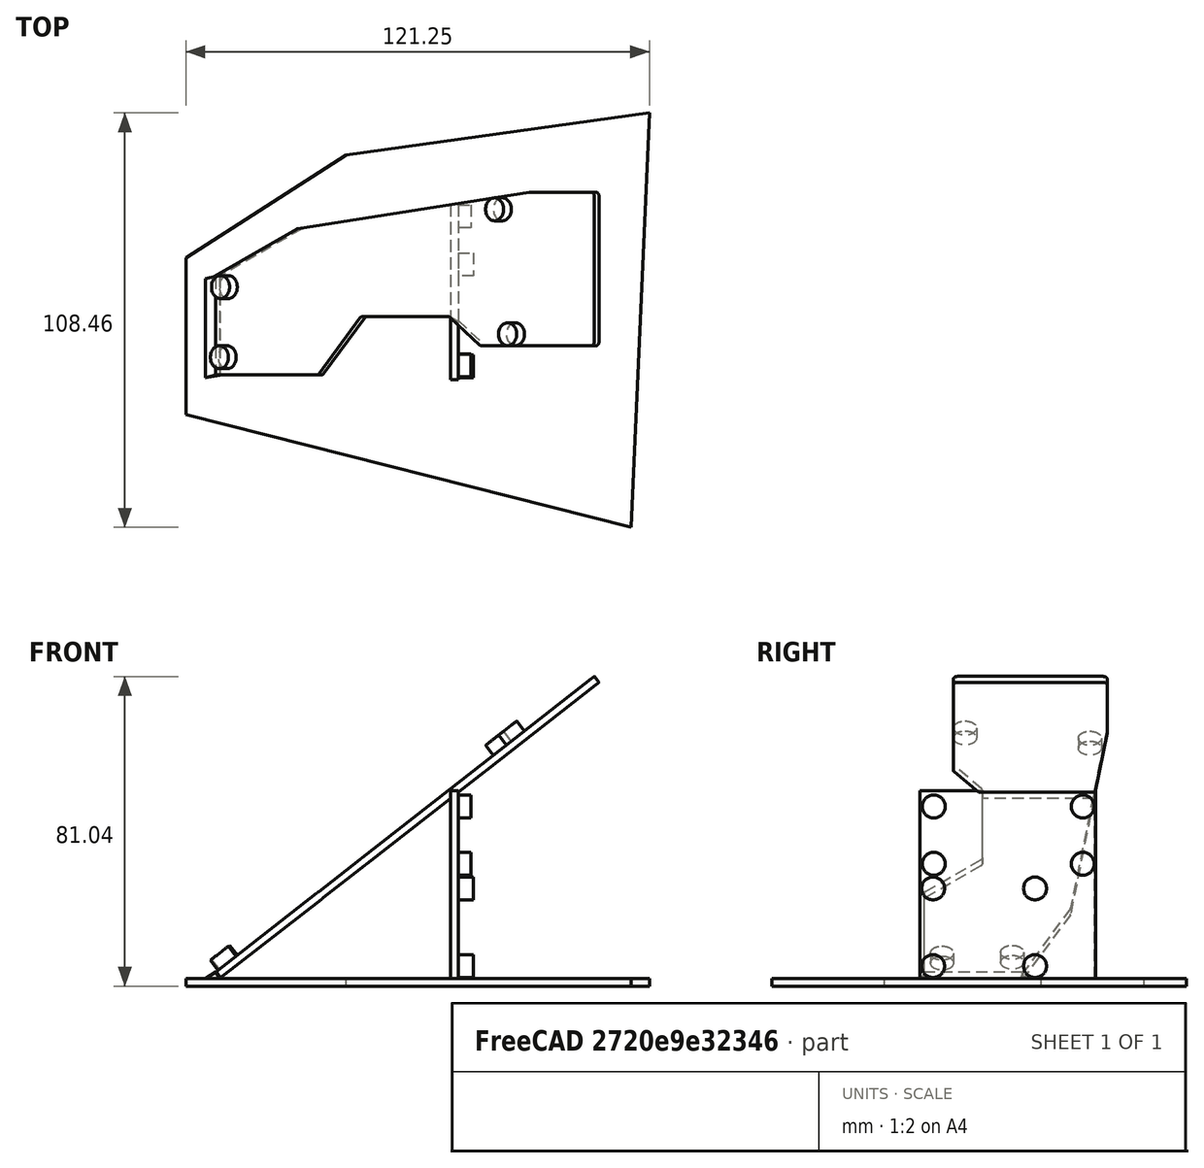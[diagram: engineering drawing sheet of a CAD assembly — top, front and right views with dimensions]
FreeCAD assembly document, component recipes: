
FREECAD ASSEMBLY — COMPONENT RECIPES ("case-tent")

This assembly document has 4 components, labeled P0..P3 below (a component is one placed body or linked part). 3 of them carry a construction recipe — the FreeCAD feature program that regenerates the part from scratch, quoted from this document or its linked companion documents; the rest are supplied as boundary geometry only. No exploded tour is included for this assembly.
COMPONENT P0 — recipe-attached ("Part001", modeled in this document).
Construction recipe (the document's own serialized feature program — sketch geometry with constraints, then the solid features built on it; lengths are millimeters unless a unit is written):

FEATURE [PartDesign::Plane] DatumPlane  label="tilt plane"
  AttachmentOffset = pos=(0,0,0) rot=(0,-1,0;0.663225rad)
  AttachmentSupport = -> [XY_Plane001]
  Length = 249.716
  MapMode = 5
  Placement = pos=(0,0,0) rot=(0,-1,0;0.663225rad)
  ResizeMode = 0
  Width = 139.285
FEATURE [Sketcher::SketchObject] PCB_Sketch_f9e006  label="left"
  ArcFitTolerance = 1e-06
  AttachmentOffset = pos=(0,3,4.4) rot=(0,0,1;0rad)
  AttachmentSupport = -> [DatumPlane]
  FullyConstrained = false
  MakeInternals = false
  MapMode = 5
  Placement = pos=(-2.70891,3,3.46725) rot=(0,-1,0;0.663225rad)
  sketch-geometry (22):
    g0: LineSegment StartX=48.9342 StartY=15.25 StartZ=0 EndX=77.5946 EndY=15.25 EndZ=0
    g1: LineSegment StartX=27.2503 StartY=38.2054 StartZ=0 EndX=0.008196 EndY=25.8215 EndZ=0
    g2: LineSegment StartX=126 StartY=8.65 StartZ=0 EndX=126 EndY=45.95 EndZ=0
    g3: LineSegment StartX=104.439 StartY=47.8424 StartZ=0 EndX=27.5489 EndY=38.289 EndZ=0
    g4: LineSegment StartX=34.5465 StartY=0.317255 StartZ=0 EndX=48.2035 EndY=14.9327 EndZ=0
    g5: LineSegment StartX=104.562 StartY=47.85 StartZ=0 EndX=125 EndY=47.85 EndZ=0
    g6: LineSegment StartX=125 StartY=7.65 StartZ=0 EndX=88.6266 EndY=7.65 EndZ=0
    g7: LineSegment StartX=0.008196 StartY=0 StartZ=0 EndX=33.8158 EndY=-1.6e-15 EndZ=0
    g8: LineSegment StartX=126 StartY=45.95 StartZ=0 EndX=126 EndY=46.85 EndZ=0
    g9: LineSegment StartX=78.291 StartY=14.9676 StartZ=0 EndX=88.0364 EndY=7.84274 EndZ=0
    g10: ArcOfCircle CenterX=27.666 CenterY=37.2959 CenterZ=0 NormalX=0 NormalY=0 NormalZ=-1 AngleXU=1.14211 Radius=1.00001 StartAngle=0 EndAngle=0.311303
    g11: ArcOfCircle CenterX=33.8158 CenterY=1.00002 CenterZ=0 NormalX=0 NormalY=0 NormalZ=-1 AngleXU=-2.39007 Radius=1.00002 StartAngle=0 EndAngle=0.81927
    g12: ArcOfCircle CenterX=48.9342 CenterY=14.25 CenterZ=0 NormalX=0 NormalY=0 NormalZ=-1 AngleXU=0.75152 Radius=1.00002 StartAngle=0 EndAngle=0.81927
    g13: ArcOfCircle CenterX=125 CenterY=46.85 CenterZ=0 NormalX=0 NormalY=0 NormalZ=-1 AngleXU=1.5708 Radius=0.999999 StartAngle=0 EndAngle=1.5708
    g14: ArcOfCircle CenterX=125 CenterY=8.65 CenterZ=0 NormalX=0 NormalY=0 NormalZ=-1 AngleXU=3.14159 Radius=0.999999 StartAngle=0 EndAngle=1.5708
    g15: ArcOfCircle CenterX=88.6266 CenterY=8.65 CenterZ=0 NormalX=0 NormalY=0 NormalZ=-1 AngleXU=-1.57079 Radius=1 StartAngle=0 EndAngle=0.631296
    g16: ArcOfCircle CenterX=104.562 CenterY=46.8498 CenterZ=0 NormalX=0 NormalY=0 NormalZ=-1 AngleXU=1.44719 Radius=1.00016 StartAngle=0 EndAngle=0.123594
    g17: ArcOfCircle CenterX=77.5946 CenterY=14.25 CenterZ=0 NormalX=0 NormalY=0 NormalZ=-1 AngleXU=1.57078 Radius=0.999961 StartAngle=0 EndAngle=0.770416
    g18: GeomPoint [constr] X=4.15 Y=4.65 Z=0
    g19: GeomPoint [constr] X=95.5 Y=43.35 Z=0
    g20: GeomPoint [constr] X=99.8333 Y=10.6833 Z=0
    g21: LineSegment StartX=0.008196 StartY=25.8215 StartZ=0 EndX=0.008196 EndY=0 EndZ=0
  constraints (20):
    c: Coincident(g1,g10)
    c: Coincident(g3,g10)
    c: Coincident(g7,g11)
    c: Coincident(g4,g11)
    c: Coincident(g4,g12)
    c: Coincident(g0,g12)
    c: Coincident(g0,g17)
    c: Coincident(g9,g17)
    c: Coincident(g9,g15)
    c: Coincident(g6,g15)
    c: Coincident(g3,g16)
    c: Coincident(g5,g16)
    c: Coincident(g6,g14)
    c: Coincident(g5,g13)
    c: Coincident(g2,g14)
    c: Coincident(g2,g8)
    c: Coincident(g8,g13)
    c: Coincident(g1,g21)
    c: Coincident(g21,g7)
    c: Vertical(g21)
FEATURE [PartDesign::Pad] Pad
  Direction = (-0.615661,0,0.788011)
  Length = 2
  Length2 = 10
  Placement = pos=(0,0,0) rot=(0,-1,0;0.663225rad)
  Profile = -> PCB_Sketch_f9e006
  ReferenceAxis = -> PCB_Sketch_f9e006 [N_Axis]
  Refine = true
  Reversed = true
  Suppressed = false
  Type = 0
FEATURE [PartDesign::Plane] DatumPlane001
  AttachmentOffset = pos=(0,0,2) rot=(0,0,1;0rad)
  AttachmentSupport = -> [XY_Plane001]
  Length = 193.247
  MapMode = 5
  Placement = pos=(0,0,2) rot=(0,0,1;0rad)
  ResizeMode = 0
  Width = 135.335
FEATURE [Sketcher::SketchObject] Sketch001
  ArcFitTolerance = 1e-06
  FullyConstrained = true
  MakeInternals = false
  MapMode = 5
  Placement = pos=(0.0069506,0,0.00434322) rot=(0.658342,-0.658342,-0.364925;2.44177rad)
  sketch-geometry (4):
    g0: LineSegment StartX=-28.8215 StartY=4.4 StartZ=0 EndX=-28.8215 EndY=2.4 EndZ=0
    g1: LineSegment StartX=-28.8215 StartY=2.4 StartZ=0 EndX=-3 EndY=2.4 EndZ=0
    g2: LineSegment StartX=-3 StartY=2.4 StartZ=0 EndX=-3 EndY=4.4 EndZ=0
    g3: LineSegment StartX=-3 StartY=4.4 StartZ=0 EndX=-28.8215 EndY=4.4 EndZ=0
  constraints (10):
    c: Coincident(g0,g1)
    c: Coincident(g1,g2)
    c: Coincident(g2,g3)
    c: Coincident(g3,g0)
    c: Vertical(g0)
    c: Vertical(g2)
    c: Horizontal(g1)
    c: Horizontal(g3)
    c: Coincident(g0,g-4)
    c: Coincident(g1,g-6)
FEATURE [PartDesign::Pad] Pad002
  BaseFeature = -> Pad
  Direction = (-0.85,-0.2,-0.53)
  Length = 10
  Length2 = 10
  Placement = pos=(0,0,0) rot=(0,-1,0;0.663225rad)
  Profile = -> Sketch001
  ReferenceAxis = -> Sketch001 [N_Axis]
  Refine = true
  Suppressed = false
  Type = 5
  UpToShape = -> [DatumPlane001]
  UseCustomVector = true
FEATURE [Sketcher::SketchObject] Sketch
  ArcFitTolerance = 1e-06
  AttachmentSupport = -> [XY_Plane001]
  FullyConstrained = false
  MakeInternals = false
  MapMode = 5
  sketch-geometry (5):
    g0: LineSegment StartX=-10.2101 StartY=33.6647 StartZ=0 EndX=-10.2101 EndY=-7.34119 EndZ=0
    g1: LineSegment StartX=-10.2101 StartY=-7.34119 StartZ=0 EndX=106.194 EndY=-36.883 EndZ=0
    g2: LineSegment StartX=106.194 StartY=-36.883 StartZ=0 EndX=111.044 EndY=71.5841 EndZ=0
    g3: LineSegment StartX=111.044 StartY=71.5841 StartZ=0 EndX=31.6776 EndY=60.561 EndZ=0
    g4: LineSegment StartX=31.6776 StartY=60.561 StartZ=0 EndX=-10.2101 EndY=33.6647 EndZ=0
  constraints (6):
    c: Vertical(g0)
    c: Coincident(g0,g1)
    c: Coincident(g1,g2)
    c: Coincident(g2,g3)
    c: Coincident(g3,g4)
    c: Coincident(g4,g0)
FEATURE [PartDesign::Pad] Pad003
  BaseFeature = -> Pad002
  Direction = (0,0,1)
  Length = 2
  Length2 = 10
  Placement = pos=(0,0,0) rot=(0,-1,0;0.663225rad)
  Profile = -> Sketch
  ReferenceAxis = -> Sketch [N_Axis]
  Refine = true
  Suppressed = false
  Type = 0
FEATURE [Sketcher::SketchObject] Sketch002
  ArcFitTolerance = 1e-06
  AttachmentSupport = -> [XY_Plane001]
  FullyConstrained = false
  MakeInternals = false
  MapMode = 5
  sketch-geometry (5):
    g0: LineSegment StartX=58.9852 StartY=17.9676 StartZ=0 EndX=58.9852 EndY=1.83853 EndZ=0
    g1: LineSegment StartX=58.9852 StartY=1.83853 StartZ=0 EndX=60.9852 EndY=1.83853 EndZ=0
    g2: LineSegment StartX=60.9852 StartY=1.83853 StartZ=0 EndX=60.9852 EndY=47.9089 EndZ=0
    g3: LineSegment StartX=60.9852 StartY=47.9089 StartZ=0 EndX=58.9852 EndY=47.5936 EndZ=0
    g4: LineSegment StartX=58.9852 StartY=47.5936 StartZ=0 EndX=58.9852 EndY=17.9676 EndZ=0
  constraints (13):
    c: Coincident(g-3,g0)
    c: Vertical(g0)
    c: Coincident(g0,g1)
    c: Horizontal(g1)
    c: Coincident(g1,g2)
    c: PointOnObject(g2,g-4)
    c: Vertical(g2)
    c: Coincident(g2,g3)
    c: PointOnObject(g3,g-4)
    c: Coincident(g3,g4)
    c: Coincident(g4,g0)
    c: Vertical(g4)
    c: DistanceX(g1,g1) = 2
FEATURE [PartDesign::Pad] Pad004
  BaseFeature = -> Pad003
  Direction = (0,0,1)
  Length = 51.1
  Length2 = 10
  Placement = pos=(0,0,0) rot=(0,-1,0;0.663225rad)
  Profile = -> Sketch002
  ReferenceAxis = -> Sketch002 [N_Axis]
  Refine = true
  Suppressed = false
  Type = 0
FEATURE [Sketcher::SketchObject] PCB_Sketch_58ce  label="thumb cluster"
  ArcFitTolerance = 1e-06
  AttachmentOffset = pos=(2.5,50,0) rot=(0,0,1;-1.5708rad)
  AttachmentSupport = -> [Pad004]
  FullyConstrained = false
  MakeInternals = false
  MapMode = 5
  Placement = pos=(60.9852,2.5,50) rot=(0,-1,0;4.71239rad)
  sketch-geometry (16):
    g0: LineSegment StartX=21 StartY=44 StartZ=0 EndX=21 EndY=1 EndZ=0
    g1: LineSegment StartX=20 StartY=1e-16 StartZ=0 EndX=1 EndY=0 EndZ=0
    g2: LineSegment StartX=1 StartY=45 StartZ=0 EndX=20 EndY=45 EndZ=0
    g3: LineSegment StartX=1e-16 StartY=1 StartZ=0 EndX=3.3e-15 EndY=44 EndZ=0
    g4: ArcOfCircle CenterX=20 CenterY=44 CenterZ=0 NormalX=0 NormalY=0 NormalZ=-1 AngleXU=1.5708 Radius=0.999999 StartAngle=0 EndAngle=1.5708
    g5: ArcOfCircle CenterX=0.999999 CenterY=0.999999 CenterZ=0 NormalX=0 NormalY=0 NormalZ=-1 AngleXU=-1.5708 Radius=0.999999 StartAngle=0 EndAngle=1.5708
    g6: ArcOfCircle CenterX=20 CenterY=0.999999 CenterZ=0 NormalX=0 NormalY=0 NormalZ=-1 AngleXU=3.14159 Radius=0.999999 StartAngle=0 EndAngle=1.5708
    g7: ArcOfCircle CenterX=0.999999 CenterY=44 CenterZ=0 NormalX=0 NormalY=0 NormalZ=-1 AngleXU=-7.47076e-07 Radius=0.999999 StartAngle=0 EndAngle=1.5708
    g8: GeomPoint [constr] X=3 Y=42 Z=0
    g9: GeomPoint [constr] X=18 Y=42 Z=0
    g10: GeomPoint [constr] X=18 Y=3 Z=0
    g11: GeomPoint [constr] X=3 Y=3 Z=0
    g12: Circle CenterX=3 CenterY=42 CenterZ=0 NormalX=0 NormalY=0 NormalZ=1 AngleXU=0 Radius=3
    g13: Circle CenterX=18 CenterY=42 CenterZ=0 NormalX=0 NormalY=0 NormalZ=1 AngleXU=0 Radius=3
    g14: Circle CenterX=18 CenterY=3 CenterZ=0 NormalX=0 NormalY=0 NormalZ=1 AngleXU=0 Radius=3
    g15: Circle CenterX=3 CenterY=3 CenterZ=0 NormalX=0 NormalY=0 NormalZ=1 AngleXU=0 Radius=3
  constraints (18):
    c: Coincident(g3,g5)
    c: Coincident(g3,g7)
    c: Coincident(g1,g5)
    c: Coincident(g2,g7)
    c: Coincident(g1,g6)
    c: Coincident(g2,g4)
    c: Coincident(g0,g6)
    c: Coincident(g0,g4)
    c: Diameter(g12) = 6
    c: Coincident(g12,g8)
    c: Diameter(g13) = 6
    c: Coincident(g13,g9)
    c: Tangent(g13,g0)
    c: Diameter(g14) = 6
    c: Coincident(g14,g10)
    c: Tangent(g14,g0)
    c: Diameter(g15) = 6
    c: Coincident(g15,g11)
FEATURE [Sketcher::SketchObject] PCB_Sketch_bbd4  label="thumbstick"
  ArcFitTolerance = 1e-06
  AttachmentOffset = pos=(40.5,2.7,0) rot=(0,0,1;1.5708rad)
  AttachmentSupport = -> [Pad004]
  FullyConstrained = false
  MakeInternals = false
  MapMode = 5
  Placement = pos=(60.9852,40.5,2.7) rot=(0.707107,0,0.707107;3.14159rad)
  sketch-geometry (12):
    g0: LineSegment StartX=0 StartY=37.72 StartZ=0 EndX=0 EndY=0 EndZ=0
    g1: LineSegment StartX=25.4 StartY=37.72 StartZ=0 EndX=0 EndY=37.72 EndZ=0
    g2: LineSegment StartX=0 StartY=0 StartZ=0 EndX=25.4 EndY=0 EndZ=0
    g3: LineSegment StartX=25.4 StartY=0 StartZ=0 EndX=25.4 EndY=37.72 EndZ=0
    g4: GeomPoint [constr] X=2.54 Y=35.18 Z=0
    g5: GeomPoint [constr] X=22.86 Y=35.18 Z=0
    g6: GeomPoint [constr] X=22.86 Y=8.51 Z=0
    g7: GeomPoint [constr] X=2.54 Y=8.51 Z=0
    g8: Circle CenterX=22.86 CenterY=35.18 CenterZ=0 NormalX=0 NormalY=0 NormalZ=1 AngleXU=0 Radius=3
    g9: Circle CenterX=2.54 CenterY=35.18 CenterZ=0 NormalX=0 NormalY=0 NormalZ=1 AngleXU=0 Radius=3
    g10: Circle CenterX=2.54 CenterY=8.51 CenterZ=0 NormalX=0 NormalY=0 NormalZ=1 AngleXU=0 Radius=3
    g11: Circle CenterX=22.86 CenterY=8.51 CenterZ=0 NormalX=0 NormalY=0 NormalZ=1 AngleXU=0 Radius=3
  constraints (12):
    c: Coincident(g0,g2)
    c: Coincident(g0,g1)
    c: Coincident(g2,g3)
    c: Coincident(g1,g3)
    c: Diameter(g8) = 6
    c: Coincident(g8,g5)
    c: Diameter(g9) = 6
    c: Coincident(g9,g4)
    c: Diameter(g10) = 6
    c: Coincident(g10,g7)
    c: Diameter(g11) = 6
    c: Coincident(g11,g6)
FEATURE [Sketcher::SketchObject] Sketch003
  ArcFitTolerance = 1e-06
  AttachmentSupport = -> [Pad004]
  FullyConstrained = false
  MakeInternals = false
  MapMode = 5
  Placement = pos=(-2.70891,0,3.46725) rot=(0,-1,0;0.663225rad)
  sketch-geometry (4):
    g0: Circle CenterX=4.49466 CenterY=26.0177 CenterZ=0 NormalX=0 NormalY=0 NormalZ=1 AngleXU=0 Radius=3
    g1: Circle CenterX=4.15 CenterY=7.65 CenterZ=0 NormalX=0 NormalY=0 NormalZ=1 AngleXU=0 Radius=3
    g2: Circle CenterX=95.5 CenterY=46.35 CenterZ=0 NormalX=0 NormalY=0 NormalZ=1 AngleXU=0 Radius=3
    g3: Circle CenterX=99.8333 CenterY=13.6833 CenterZ=0 NormalX=0 NormalY=0 NormalZ=1 AngleXU=0 Radius=3
FEATURE [PartDesign::Pad] Pad005
  BaseFeature = -> Pad004
  Direction = (-0.615661,0,0.788011)
  Length = 3.3
  Length2 = 10
  Placement = pos=(0,0,0) rot=(0,-1,0;0.663225rad)
  Profile = -> Sketch003
  ReferenceAxis = -> Sketch003 [N_Axis]
  Refine = true
  Suppressed = false
  Type = 0
FEATURE [Sketcher::SketchObject] Sketch004
  ArcFitTolerance = 1e-06
  AttachmentSupport = -> [Pad005]
  ExternalGeometry = -> [PCB_Sketch_58ce]
  FullyConstrained = true
  MakeInternals = false
  MapMode = 5
  Placement = pos=(60.9852,0,4.74e-14) rot=(0.57735,0.57735,0.57735;2.0944rad)
  sketch-geometry (4):
    g0: Circle CenterX=5.5 CenterY=47 CenterZ=0 NormalX=0 NormalY=0 NormalZ=1 AngleXU=0 Radius=3
    g1: Circle CenterX=44.5 CenterY=47 CenterZ=0 NormalX=0 NormalY=0 NormalZ=1 AngleXU=0 Radius=3
    g2: Circle CenterX=44.5 CenterY=32 CenterZ=0 NormalX=0 NormalY=0 NormalZ=1 AngleXU=0 Radius=3
    g3: Circle CenterX=5.5 CenterY=32 CenterZ=0 NormalX=0 NormalY=0 NormalZ=1 AngleXU=0 Radius=3
  constraints (8):
    c: Coincident(g0,g-3)
    c: Equal(g0,g-3)
    c: Coincident(g1,g-4)
    c: Equal(g1,g-4)
    c: Coincident(g2,g-5)
    c: Equal(g2,g-5)
    c: Coincident(g3,g-6)
    c: Equal(g3,g-6)
FEATURE [PartDesign::Pad] Pad006
  BaseFeature = -> Pad005
  Direction = (1,0,0)
  Length = 3.3
  Length2 = 10
  Placement = pos=(0,0,0) rot=(0,-1,0;0.663225rad)
  Profile = -> Sketch004
  ReferenceAxis = -> Sketch004 [N_Axis]
  Refine = true
  Suppressed = false
  Type = 0
FEATURE [Sketcher::SketchObject] Sketch005
  ArcFitTolerance = 1e-06
  AttachmentSupport = -> [Pad006]
  ExternalGeometry = -> [PCB_Sketch_bbd4]
  FullyConstrained = true
  MakeInternals = false
  MapMode = 5
  Placement = pos=(60.9852,0,7.45e-14) rot=(0.57735,0.57735,0.57735;2.0944rad)
  sketch-geometry (4):
    g0: Circle CenterX=5.32 CenterY=25.56 CenterZ=0 NormalX=0 NormalY=0 NormalZ=1 AngleXU=0 Radius=3
    g1: Circle CenterX=31.99 CenterY=25.56 CenterZ=0 NormalX=0 NormalY=0 NormalZ=1 AngleXU=0 Radius=3
    g2: Circle CenterX=31.99 CenterY=5.24 CenterZ=0 NormalX=0 NormalY=0 NormalZ=1 AngleXU=0 Radius=3
    g3: Circle CenterX=5.32 CenterY=5.24 CenterZ=0 NormalX=0 NormalY=0 NormalZ=1 AngleXU=0 Radius=3
  constraints (8):
    c: Coincident(g0,g-3)
    c: Equal(g0,g-3)
    c: Coincident(g1,g-5)
    c: Equal(g1,g-5)
    c: Coincident(g2,g-6)
    c: Equal(g2,g-6)
    c: Coincident(g3,g-4)
    c: Equal(g3,g-4)
FEATURE [PartDesign::Pad] Pad007
  BaseFeature = -> Pad006
  Direction = (1,0,1.3e-15)
  Length = 4
  Length2 = 10
  Placement = pos=(0,0,0) rot=(0,-1,0;0.663225rad)
  Profile = -> Sketch005
  ReferenceAxis = -> Sketch005 [N_Axis]
  Refine = true
  Suppressed = false
  Type = 0
FEATURE [PartDesign::Body] Body
  AllowCompound = false
  Group = -> [DatumPlane,PCB_Sketch_f9e006,Pad,PCB_Sketch_58ce,DatumPlane001,PCB_Sketch_bbd4,Sketch001,Pad002,Sketch,Pad003,Sketch002,Pad004,Sketch003,Pad005,Sketch004,Pad006,Sketch005,Pad007]
  Origin = -> Origin001
  Tip = -> Pad007
COMPONENT P1 — geometry summary ("left001"; no construction recipe available for this part):
  bounding box: 100.3 x 81.8 x 48.0 mm
  tessellated surface: 115,676 triangles
  volume: 8489 mm^3 (2% of its bounding box)
COMPONENT P2 — recipe-attached ("thumb-cluster", a linked part whose construction recipe lives in a companion FreeCAD document of the same project; that document's serialized recipe follows).
Construction recipe (the companion document, serialized — sketch geometry with constraints, then the solid features built on it; lengths are millimeters unless a unit is written):

FCSTD DOCUMENT  (FreeCAD 1.0RUnknown)
Label: thumb-cluster
License: All rights reserved
LicenseURL: https://en.wikipedia.org/wiki/All_rights_reserved
objects: Part::Feature×14, Sketcher::SketchObject×10, App::Link×10, App::Part×6, PartDesign::Pocket×4, PartDesign::Pad×3, PartDesign::Chamfer×3, PartDesign::Thickness×2, PartDesign::Body×2, PartDesign::SubShapeBinder×2, PartDesign::CoordinateSystem×1, PartDesign::ShapeBinder×1
note: 76 computed .brp shape members not serialized (recipe doc carries the construction recipe); baked Part::Feature solids carry a one-line shape summary decoded from their .brp

FEATURE [PartDesign::CoordinateSystem] Local_CS_58ce
  AttacherType = Attacher::AttachEngine3D
  MapMode = 2
FEATURE [Part::Feature] Pcb_58ce
  Placement = pos=(-19.5,69,0) rot=(0,0,1;0rad)
  shape: bbox 21 x 45 x 1.6 mm, 50 faces (baked)
FEATURE [Sketcher::SketchObject] PCB_Sketch_58ce
  ArcFitTolerance = 1e-06
  FullyConstrained = false
  MakeInternals = false
  sketch-geometry (8):
    g0: LineSegment StartX=21 StartY=44 StartZ=0 EndX=21 EndY=1 EndZ=0
    g1: LineSegment StartX=20 StartY=1e-16 StartZ=0 EndX=1 EndY=0 EndZ=0
    g2: LineSegment StartX=1 StartY=45 StartZ=0 EndX=20 EndY=45 EndZ=0
    g3: LineSegment StartX=1e-16 StartY=1 StartZ=0 EndX=3.3e-15 EndY=44 EndZ=0
    g4: ArcOfCircle CenterX=20 CenterY=44 CenterZ=0 NormalX=0 NormalY=0 NormalZ=-1 AngleXU=1.5708 Radius=0.999999 StartAngle=0 EndAngle=1.5708
    g5: ArcOfCircle CenterX=0.999999 CenterY=0.999999 CenterZ=0 NormalX=0 NormalY=0 NormalZ=-1 AngleXU=-1.5708 Radius=0.999999 StartAngle=0 EndAngle=1.5708
    g6: ArcOfCircle CenterX=20 CenterY=0.999999 CenterZ=0 NormalX=0 NormalY=0 NormalZ=-1 AngleXU=3.14159 Radius=0.999999 StartAngle=0 EndAngle=1.5708
    g7: ArcOfCircle CenterX=0.999999 CenterY=44 CenterZ=0 NormalX=0 NormalY=0 NormalZ=-1 AngleXU=-7.47076e-07 Radius=0.999999 StartAngle=0 EndAngle=1.5708
  constraints (8):
    c: Coincident(g3,g5)
    c: Coincident(g3,g7)
    c: Coincident(g1,g5)
    c: Coincident(g2,g7)
    c: Coincident(g1,g6)
    c: Coincident(g2,g4)
    c: Coincident(g0,g6)
    c: Coincident(g0,g4)
FEATURE [App::Part] Board_Geoms_58ce
  Group = -> [Pcb_58ce,PCB_Sketch_58ce]
  Origin = -> Origin
FEATURE [Part::Feature] Shape  label="D24_D_SOD_123_0f779e6ff9e7"
  Placement = pos=(3.66673,13.8333,0) rot=(0,0,-1;0.785398rad)
  shape: bbox 3.147 x 3.147 x 1.25 mm, 67 faces (baked)
FEATURE [Part::Feature] Shape001  label="J4_SOLID_42e36dcc9d63"
  Placement = pos=(10.9645,42.4,0) rot=(0,0.707107,0.707107;3.14159rad)
  shape: bbox 5.501 x 4.001 x 0.9009 mm, 979 faces (baked)
FEATURE [App::Link] D24_D_SOD_123_0f779e6ff9e7_ln_  label="D23_D_SOD_123_3fd67df90355"
  LinkPlacement = pos=(5.66673,15.8333,0) rot=(0,0,-1;0.785398rad)
  LinkedObject = -> Shape
  Placement = pos=(5.66673,15.8333,0) rot=(0,0,-1;0.785398rad)
FEATURE [App::Link] D24_D_SOD_123_0f779e6ff9e7_ln_001  label="D30_D_SOD_123_61e72e2af53f"
  LinkPlacement = pos=(19.75,16.55,0) rot=(0,0,-1;1.5708rad)
  LinkedObject = -> Shape
  Placement = pos=(19.75,16.55,0) rot=(0,0,-1;1.5708rad)
FEATURE [App::Link] D24_D_SOD_123_0f779e6ff9e7_ln_002  label="D27_D_SOD_123_7b2efe9b5669"
  LinkPlacement = pos=(17.6667,24.3333,0) rot=(0,0,1;2.35619rad)
  LinkedObject = -> Shape
  Placement = pos=(17.6667,24.3333,0) rot=(0,0,1;2.35619rad)
FEATURE [App::Link] D24_D_SOD_123_0f779e6ff9e7_ln_003  label="D22_D_SOD_123_057a97edfa83"
  LinkPlacement = pos=(7.66673,17.8333,0) rot=(0,0,-1;0.785398rad)
  LinkedObject = -> Shape
  Placement = pos=(7.66673,17.8333,0) rot=(0,0,-1;0.785398rad)
FEATURE [App::Link] D24_D_SOD_123_0f779e6ff9e7_ln_004  label="D29_D_SOD_123_cdf521000048"
  LinkPlacement = pos=(16.5,16.55,0) rot=(0,0,-1;1.5708rad)
  LinkedObject = -> Shape
  Placement = pos=(16.5,16.55,0) rot=(0,0,-1;1.5708rad)
FEATURE [App::Link] D24_D_SOD_123_0f779e6ff9e7_ln_005  label="D28_D_SOD_123_d5d7d507dfc1"
  LinkPlacement = pos=(15.6667,22.3333,0) rot=(0,0,1;2.35619rad)
  LinkedObject = -> Shape
  Placement = pos=(15.6667,22.3333,0) rot=(0,0,1;2.35619rad)
FEATURE [App::Link] D24_D_SOD_123_0f779e6ff9e7_ln_006  label="D20_D_SOD_123_675b5f77a9ad"
  LinkPlacement = pos=(5.16673,33.8333,0) rot=(0,0,-1;0.785398rad)
  LinkedObject = -> Shape
  Placement = pos=(5.16673,33.8333,0) rot=(0,0,-1;0.785398rad)
FEATURE [Part::Feature] Part__Feature  label="SKRHAD"
  shape: bbox 7.483 x 7.5 x 5.5 mm, 242 faces (baked)
FEATURE [Part::Feature] Part__Feature001  label="Pins"
  shape: bbox 1.15 x 0.8 x 0.1 mm, 6 faces (baked)
FEATURE [Part::Feature] Part__Feature002  label="Pins001"
  shape: bbox 1.15 x 0.8 x 0.1 mm, 6 faces (baked)
FEATURE [Part::Feature] Part__Feature003  label="Pins002"
  shape: bbox 1.15 x 0.8 x 0.1 mm, 6 faces (baked)
FEATURE [Part::Feature] Part__Feature004  label="Pins003"
  shape: bbox 1.15 x 0.8 x 0.1 mm, 6 faces (baked)
FEATURE [Part::Feature] Part__Feature005  label="Pins004"
  shape: bbox 1.15 x 0.8 x 0.1 mm, 6 faces (baked)
FEATURE [Part::Feature] Part__Feature006  label="Pins005"
  shape: bbox 1.15 x 0.8 x 0.1 mm, 6 faces (baked)
FEATURE [Part::Feature] Part__Feature007  label="Pins006"
  shape: bbox 1.64 x 1.44 x 0.1 mm, 6 faces (baked)
FEATURE [Part::Feature] Part__Feature008  label="Pins007"
  shape: bbox 1.64 x 1.44 x 0.1 mm, 6 faces (baked)
FEATURE [Part::Feature] Part__Feature009  label="Lugs"
  shape: bbox 0.55 x 0.55 x 1.8 mm, 3 faces (baked)
FEATURE [Part::Feature] Part__Feature010  label="Lugs001"
  shape: bbox 0.85 x 0.85 x 1.8 mm, 3 faces (baked)
FEATURE [App::Part] SKRHADE  label="S6_SKRHADE_66ce9957abdd"
  Group = -> [Part__Feature,Part__Feature001,Part__Feature002,Part__Feature003,Part__Feature004,Part__Feature005,Part__Feature006,Part__Feature007,Part__Feature008,Part__Feature009,Part__Feature010]
  Origin = -> Origin008
  Placement = pos=(10.9645,9.96447,0) rot=(0,0,-1;0.785398rad)
FEATURE [App::Link] D24_D_SOD_123_0f779e6ff9e7_ln_007  label="D21_D_SOD_123_014bcfdeeddd"
  LinkPlacement = pos=(3.16673,31.8333,0) rot=(0,0,-1;0.785398rad)
  LinkedObject = -> Shape
  Placement = pos=(3.16673,31.8333,0) rot=(0,0,-1;0.785398rad)
FEATURE [App::Link] D24_D_SOD_123_0f779e6ff9e7_ln_008  label="D19_D_SOD_123_2a26592c9c0c"
  LinkPlacement = pos=(7.16673,35.8333,0) rot=(0,0,-1;0.785398rad)
  LinkedObject = -> Shape
  Placement = pos=(7.16673,35.8333,0) rot=(0,0,-1;0.785398rad)
FEATURE [App::Link] S6_SKRHADE_66ce9957abdd_ln_  label="S5_SKRHADE_e4e283c67a98"
  LinkPlacement = pos=(10.9645,28.5203,0) rot=(0,0,-1;0.785398rad)
  LinkedObject = -> SKRHADE
  Placement = pos=(10.9645,28.5203,0) rot=(0,0,-1;0.785398rad)
FEATURE [App::Part] Top_58ce
  Group = -> [Shape,Shape001,D24_D_SOD_123_0f779e6ff9e7_ln_,D24_D_SOD_123_0f779e6ff9e7_ln_001,D24_D_SOD_123_0f779e6ff9e7_ln_002,D24_D_SOD_123_0f779e6ff9e7_ln_003,D24_D_SOD_123_0f779e6ff9e7_ln_004,D24_D_SOD_123_0f779e6ff9e7_ln_005,D24_D_SOD_123_0f779e6ff9e7_ln_006,SKRHADE,D24_D_SOD_123_0f779e6ff9e7_ln_007,D24_D_SOD_123_0f779e6ff9e7_ln_008,S6_SKRHADE_66ce9957abdd_ln_]
  Origin = -> Origin003
FEATURE [App::Part] Step_Models_58ce
  Group = -> [Top_58ce]
  Origin = -> Origin002
FEATURE [Sketcher::SketchObject] Sketch  label="2.2"
  ArcFitTolerance = 1e-06
  FullyConstrained = false
  MakeInternals = false
  Placement = pos=(0,0,0) rot=(0,0,1;3.14159rad)
  sketch-geometry (8):
    g0: LineSegment StartX=-23.2 StartY=-44 StartZ=0 EndX=-23.2 EndY=-0.999999 EndZ=0
    g1: ArcOfCircle CenterX=-20 CenterY=-0.999999 CenterZ=0 NormalX=0 NormalY=0 NormalZ=1 AngleXU=-3.14159 Radius=3.2 StartAngle=4.71239 EndAngle=6.28318
    g2: LineSegment StartX=-20 StartY=2.2 StartZ=0 EndX=-0.999999 EndY=2.2 EndZ=0
    g3: ArcOfCircle CenterX=-0.999999 CenterY=-0.999999 CenterZ=0 NormalX=0 NormalY=0 NormalZ=1 AngleXU=1.5708 Radius=3.2 StartAngle=4.71239 EndAngle=6.28318
    g4: LineSegment StartX=2.2 StartY=-0.999999 StartZ=0 EndX=2.2 EndY=-44 EndZ=0
    g5: ArcOfCircle CenterX=-0.999999 CenterY=-44 CenterZ=0 NormalX=0 NormalY=0 NormalZ=1 AngleXU=7.47076e-07 Radius=3.2 StartAngle=4.71239 EndAngle=6.28318
    g6: LineSegment StartX=-0.999999 StartY=-47.2 StartZ=0 EndX=-20 EndY=-47.2 EndZ=0
    g7: ArcOfCircle CenterX=-20 CenterY=-44 CenterZ=0 NormalX=0 NormalY=0 NormalZ=1 AngleXU=-1.5708 Radius=3.2 StartAngle=4.71239 EndAngle=6.28318
  constraints (12):
    c: Vertical(g0)
    c: Coincident(g0,g1)
    c: Coincident(g1,g2)
    c: Horizontal(g2)
    c: Coincident(g2,g3)
    c: Coincident(g3,g4)
    c: Vertical(g4)
    c: Coincident(g4,g5)
    c: Coincident(g5,g6)
    c: Horizontal(g6)
    c: Coincident(g6,g7)
    c: Coincident(g7,g0)
FEATURE [Sketcher::SketchObject] Sketch025  label="2.003"
  ArcFitTolerance = 1e-06
  FullyConstrained = false
  MakeInternals = false
  Placement = pos=(0,0,0) rot=(0,0,1;3.14159rad)
  sketch-geometry (8):
    g0: LineSegment StartX=-23.4 StartY=-44 StartZ=0 EndX=-23.4 EndY=-0.999999 EndZ=0
    g1: ArcOfCircle CenterX=-20 CenterY=-0.999999 CenterZ=0 NormalX=0 NormalY=0 NormalZ=1 AngleXU=0 Radius=3.4 StartAngle=1.5708 EndAngle=3.14159
    g2: LineSegment StartX=-20 StartY=2.4 StartZ=0 EndX=-0.999999 EndY=2.4 EndZ=0
    g3: ArcOfCircle CenterX=-0.999999 CenterY=-0.999999 CenterZ=0 NormalX=0 NormalY=0 NormalZ=1 AngleXU=0 Radius=3.4 StartAngle=6.28318 EndAngle=7.85398
    g4: LineSegment StartX=2.4 StartY=-1 StartZ=0 EndX=2.4 EndY=-44 EndZ=0
    g5: ArcOfCircle CenterX=-0.999999 CenterY=-44 CenterZ=0 NormalX=0 NormalY=0 NormalZ=1 AngleXU=0 Radius=3.4 StartAngle=4.71239 EndAngle=6.28318
    g6: LineSegment StartX=-0.999999 StartY=-47.4 StartZ=0 EndX=-20 EndY=-47.4 EndZ=0
    g7: ArcOfCircle CenterX=-20 CenterY=-44 CenterZ=0 NormalX=0 NormalY=0 NormalZ=1 AngleXU=0 Radius=3.4 StartAngle=3.14159 EndAngle=4.71239
  constraints (12):
    c: Vertical(g0)
    c: Coincident(g0,g1)
    c: Coincident(g1,g2)
    c: Horizontal(g2)
    c: Coincident(g2,g3)
    c: Coincident(g3,g4)
    c: Vertical(g4)
    c: Coincident(g4,g5)
    c: Coincident(g5,g6)
    c: Horizontal(g6)
    c: Coincident(g6,g7)
    c: Coincident(g7,g0)
FEATURE [PartDesign::Pad] Pad
  Direction = (0,0,1)
  Length = 3.2
  Length2 = 10
  Placement = pos=(0,0,0) rot=(0,0,1;3.14159rad)
  Profile = -> Sketch025
  ReferenceAxis = -> Sketch025 [N_Axis]
  Refine = true
  Suppressed = false
  Type = 0
FEATURE [PartDesign::Thickness] Thickness
  Base = -> Pad [Face10]
  BaseFeature = -> Pad
  Intersection = false
  Join = 0
  Mode = 0
  Refine = true
  Reversed = true
  SupportTransform = false
  Suppressed = false
  Value = 2
FEATURE [PartDesign::ShapeBinder] ShapeBinder
  Support = -> [Pcb_58ce]
  TraceSupport = false
FEATURE [Sketcher::SketchObject] Sketch026
  ArcFitTolerance = 1e-06
  AttachmentSupport = -> [Thickness]
  ExternalGeometry = -> [ShapeBinder]
  FullyConstrained = true
  MakeInternals = false
  MapMode = 5
  Placement = pos=(0,0,0) rot=(1,0,0;3.14159rad)
  sketch-geometry (4):
    g0: Circle CenterX=3 CenterY=-3 CenterZ=0 NormalX=0 NormalY=0 NormalZ=1 AngleXU=0 Radius=1.25
    g1: Circle CenterX=18 CenterY=-3 CenterZ=0 NormalX=0 NormalY=0 NormalZ=1 AngleXU=0 Radius=1.25
    g2: Circle CenterX=18 CenterY=-42 CenterZ=0 NormalX=0 NormalY=0 NormalZ=1 AngleXU=0 Radius=1.25
    g3: Circle CenterX=3 CenterY=-42 CenterZ=0 NormalX=0 NormalY=0 NormalZ=1 AngleXU=0 Radius=1.25
  constraints (8):
    c: Coincident(g0,g-3)
    c: Coincident(g1,g-4)
    c: Coincident(g2,g-5)
    c: Diameter(g2) = 2.5
    c: Equal(g0,g1)
    c: Equal(g1,g2)
    c: Coincident(g3,g-6)
    c: Equal(g2,g3)
FEATURE [PartDesign::Pocket] Pocket010
  BaseFeature = -> Thickness
  Direction = (0,0,1)
  Length = 5
  Length2 = 5
  Profile = -> Sketch026
  ReferenceAxis = -> Sketch026 [N_Axis]
  Refine = true
  Suppressed = false
  Type = 1
FEATURE [PartDesign::Chamfer] Chamfer001
  Angle = 60
  Base = -> Pocket010 [Edge18,Edge19,Edge16,Edge17]
  BaseFeature = -> Pocket010
  ChamferType = 2
  FlipDirection = false
  Refine = true
  Size = 0.8
  Size2 = 1
  SupportTransform = false
  Suppressed = false
  UseAllEdges = false
FEATURE [PartDesign::Body] Body010  label="base"
  AllowCompound = false
  Group = -> [Sketch025,Pad,Thickness,ShapeBinder,Sketch026,Pocket010,Chamfer001]
  Origin = -> Origin022
  Placement = pos=(0,0,-3.6) rot=(0,0,1;0rad)
  Tip = -> Chamfer001
FEATURE [Sketcher::SketchObject] Sketch027  label="2.004"
  ArcFitTolerance = 1e-06
  FullyConstrained = false
  MakeInternals = false
  Placement = pos=(0,0,0) rot=(0,0,1;3.14159rad)
  sketch-geometry (8):
    g0: LineSegment StartX=-23.4 StartY=-44 StartZ=0 EndX=-23.4 EndY=-1 EndZ=0
    g1: ArcOfCircle CenterX=-20 CenterY=-0.999999 CenterZ=0 NormalX=0 NormalY=0 NormalZ=1 AngleXU=0 Radius=3.4 StartAngle=1.5708 EndAngle=3.14159
    g2: LineSegment StartX=-20 StartY=2.4 StartZ=0 EndX=-1 EndY=2.4 EndZ=0
    g3: ArcOfCircle CenterX=-0.999999 CenterY=-0.999999 CenterZ=0 NormalX=0 NormalY=0 NormalZ=1 AngleXU=0 Radius=3.4 StartAngle=6.28318 EndAngle=7.85398
    g4: LineSegment StartX=2.4 StartY=-1 StartZ=0 EndX=2.4 EndY=-44 EndZ=0
    g5: ArcOfCircle CenterX=-0.999999 CenterY=-44 CenterZ=0 NormalX=0 NormalY=0 NormalZ=1 AngleXU=0 Radius=3.4 StartAngle=4.71239 EndAngle=6.28319
    g6: LineSegment StartX=-0.999999 StartY=-47.4 StartZ=0 EndX=-20 EndY=-47.4 EndZ=0
    g7: ArcOfCircle CenterX=-20 CenterY=-44 CenterZ=0 NormalX=0 NormalY=0 NormalZ=1 AngleXU=0 Radius=3.4 StartAngle=3.14159 EndAngle=4.71239
  constraints (12):
    c: Vertical(g0)
    c: Coincident(g0,g1)
    c: Coincident(g1,g2)
    c: Horizontal(g2)
    c: Coincident(g2,g3)
    c: Coincident(g3,g4)
    c: Vertical(g4)
    c: Coincident(g4,g5)
    c: Coincident(g5,g6)
    c: Horizontal(g6)
    c: Coincident(g6,g7)
    c: Coincident(g7,g0)
FEATURE [PartDesign::Pad] Pad014
  Direction = (0,0,1)
  Length = 5
  Length2 = 10
  Placement = pos=(0,0,0) rot=(0,0,1;3.14159rad)
  Profile = -> Sketch027
  ReferenceAxis = -> Sketch027 [N_Axis]
  Refine = true
  Suppressed = false
  Type = 0
FEATURE [PartDesign::Thickness] Thickness001
  Base = -> Pad014 [Face9]
  BaseFeature = -> Pad014
  Intersection = false
  Join = 0
  Mode = 0
  Refine = true
  Reversed = true
  SupportTransform = false
  Suppressed = false
  Value = 2
FEATURE [PartDesign::SubShapeBinder] Binder001
  BindCopyOnChange = 0
  BindMode = 0
  ClaimChildren = false
  Context = -> Board_58ce [Part001.Body011.Binder001.]
  Fuse = false
  MakeFace = true
  OffsetFill = false
  OffsetIntersection = false
  OffsetJoinType = 0
  OffsetOpenResult = false
  PartialLoad = false
  Refine = true
  Relative = true
  Support = -> [Step_Models_58ce[Top_58ce.S6_SKRHADE_66ce9957abdd_ln_.Part__Feature.Edge656,Top_58ce.S6_SKRHADE_66ce9957abdd_ln_.Part__Feature.Edge660,Top_58ce.SKRHADE.Part__Feature.Edge656,Top_58ce.SKRHADE.Part__Feature.Edge660]]
  _Version = 2
FEATURE [Sketcher::SketchObject] Sketch029
  ArcFitTolerance = 1e-06
  AttachmentSupport = -> [Thickness001]
  ExternalGeometry = -> [Binder001]
  FullyConstrained = false
  MakeInternals = false
  MapMode = 5
  Placement = pos=(0,0,5) rot=(0,0,1;0rad)
  sketch-geometry (6):
    g0: LineSegment [constr] StartX=11.8395 StartY=28.5203 StartZ=0 EndX=10.4199 EndY=28.5203 EndZ=0
    g1: LineSegment [constr] StartX=10.9645 StartY=27.6453 StartZ=0 EndX=10.9645 EndY=28.5203 EndZ=0
    g2: LineSegment [constr] StartX=11.8395 StartY=9.96447 StartZ=0 EndX=10.2544 EndY=9.96447 EndZ=0
    g3: LineSegment [constr] StartX=10.9645 StartY=9.08947 StartZ=0 EndX=10.9645 EndY=9.96447 EndZ=0
    g4: Circle CenterX=10.9645 CenterY=9.96447 CenterZ=0 NormalX=0 NormalY=0 NormalZ=1 AngleXU=0 Radius=4.5
    g5: Circle CenterX=10.9645 CenterY=28.5203 CenterZ=0 NormalX=0 NormalY=0 NormalZ=1 AngleXU=0 Radius=4.5
  constraints (14):
    c: Symmetric(g-4,g-4,g0)
    c: Horizontal(g0)
    c: Symmetric(g-3,g-3,g1)
    c: PointOnObject(g1,g0)
    c: Vertical(g1)
    c: Symmetric(g-6,g-6,g2)
    c: Horizontal(g2)
    c: Symmetric(g-5,g-5,g3)
    c: PointOnObject(g3,g2)
    c: Vertical(g3)
    c: Diameter(g4) = 9
    c: Coincident(g4,g3)
    c: Diameter(g5) = 9
    c: Coincident(g5,g1)
FEATURE [PartDesign::Pocket] Pocket011
  BaseFeature = -> Thickness001
  Direction = (0,0,-1)
  Length = 5
  Length2 = 5
  Profile = -> Sketch029
  ReferenceAxis = -> Sketch029 [N_Axis]
  Refine = true
  Suppressed = false
  Type = 1
FEATURE [PartDesign::SubShapeBinder] Binder002
  BindCopyOnChange = 0
  BindMode = 0
  ClaimChildren = false
  Context = -> Board_58ce [Part001.Body011.Binder002.]
  Fuse = false
  MakeFace = true
  OffsetFill = false
  OffsetIntersection = false
  OffsetJoinType = 0
  OffsetOpenResult = false
  PartialLoad = false
  Refine = true
  Relative = true
  Support = -> [Board_Geoms_58ce[Pcb_58ce.Edge35,Pcb_58ce.Edge101,Pcb_58ce.Edge134,Pcb_58ce.Edge71]]
  _Version = 2
FEATURE [Sketcher::SketchObject] Sketch030
  ArcFitTolerance = 1e-06
  AttachmentSupport = -> [Pocket011]
  ExternalGeometry = -> [Binder002]
  FullyConstrained = true
  MakeInternals = false
  MapMode = 5
  Placement = pos=(0,0,0) rot=(1,0,0;3.14159rad)
  sketch-geometry (4):
    g0: Circle CenterX=3 CenterY=-3 CenterZ=0 NormalX=0 NormalY=0 NormalZ=1 AngleXU=0 Radius=3
    g1: Circle CenterX=18 CenterY=-3 CenterZ=0 NormalX=0 NormalY=0 NormalZ=1 AngleXU=0 Radius=3
    g2: Circle CenterX=18 CenterY=-42 CenterZ=0 NormalX=0 NormalY=0 NormalZ=1 AngleXU=0 Radius=3
    g3: Circle CenterX=3 CenterY=-42 CenterZ=0 NormalX=0 NormalY=0 NormalZ=1 AngleXU=0 Radius=3
  constraints (8):
    c: Diameter(g0) = 6
    c: Coincident(g0,g-3)
    c: Diameter(g1) = 6
    c: Coincident(g1,g-4)
    c: Diameter(g2) = 6
    c: Coincident(g2,g-5)
    c: Diameter(g3) = 6
    c: Coincident(g3,g-6)
FEATURE [PartDesign::Pad] Pad015
  BaseFeature = -> Pocket011
  Direction = (0,0,-1)
  Length = 10
  Length2 = 10
  Profile = -> Sketch030
  ReferenceAxis = -> Sketch030 [N_Axis]
  Refine = true
  Suppressed = false
  Type = 3
  UpToFace = -> Pocket011 [Face21]
FEATURE [Sketcher::SketchObject] Sketch031
  ArcFitTolerance = 1e-06
  AttachmentSupport = -> [Pad015]
  ExternalGeometry = -> [Pad015]
  FullyConstrained = true
  MakeInternals = false
  MapMode = 5
  Placement = pos=(0,0,0) rot=(1,0,0;3.14159rad)
  sketch-geometry (4):
    g0: Circle CenterX=3 CenterY=-3 CenterZ=0 NormalX=0 NormalY=0 NormalZ=1 AngleXU=0 Radius=1.65
    g1: Circle CenterX=18 CenterY=-3 CenterZ=0 NormalX=0 NormalY=0 NormalZ=1 AngleXU=0 Radius=1.65
    g2: Circle CenterX=18 CenterY=-42 CenterZ=0 NormalX=0 NormalY=0 NormalZ=1 AngleXU=0 Radius=1.65
    g3: Circle CenterX=3 CenterY=-42 CenterZ=0 NormalX=0 NormalY=0 NormalZ=1 AngleXU=0 Radius=1.65
  constraints (8):
    c: Diameter(g0) = 3.3
    c: Coincident(g0,g-3)
    c: Diameter(g1) = 3.3
    c: Coincident(g1,g-4)
    c: Diameter(g2) = 3.3
    c: Coincident(g2,g-5)
    c: Diameter(g3) = 3.3
    c: Coincident(g3,g-6)
FEATURE [PartDesign::Pocket] Pocket012
  BaseFeature = -> Pad015
  Direction = (0,0,1)
  Length = 3.3
  Length2 = 5
  Profile = -> Sketch031
  ReferenceAxis = -> Sketch031 [N_Axis]
  Refine = true
  Suppressed = false
  Type = 0
FEATURE [Sketcher::SketchObject] Sketch032
  ArcFitTolerance = 1e-06
  FullyConstrained = false
  MakeInternals = false
  Placement = pos=(0,0,0) rot=(0,0,1;3.14159rad)
  sketch-geometry (8):
    g0: LineSegment StartX=-23.4 StartY=-44 StartZ=0 EndX=-23.4 EndY=-0.999999 EndZ=0
    g1: ArcOfCircle CenterX=-20 CenterY=-0.999999 CenterZ=0 NormalX=0 NormalY=0 NormalZ=1 AngleXU=-3.14159 Radius=3.4 StartAngle=4.71239 EndAngle=6.28318
    g2: LineSegment StartX=-20 StartY=2.4 StartZ=0 EndX=-0.999999 EndY=2.4 EndZ=0
    g3: ArcOfCircle CenterX=-0.999999 CenterY=-0.999999 CenterZ=0 NormalX=0 NormalY=0 NormalZ=1 AngleXU=1.5708 Radius=3.4 StartAngle=4.71239 EndAngle=6.28318
    g4: LineSegment StartX=2.4 StartY=-0.999999 StartZ=0 EndX=2.4 EndY=-44 EndZ=0
    g5: ArcOfCircle CenterX=-0.999999 CenterY=-44 CenterZ=0 NormalX=0 NormalY=0 NormalZ=1 AngleXU=7.47076e-07 Radius=3.4 StartAngle=4.71239 EndAngle=6.28318
    g6: LineSegment StartX=-0.999999 StartY=-47.4 StartZ=0 EndX=-20 EndY=-47.4 EndZ=0
    g7: ArcOfCircle CenterX=-20 CenterY=-44 CenterZ=0 NormalX=0 NormalY=0 NormalZ=1 AngleXU=-1.5708 Radius=3.4 StartAngle=4.71239 EndAngle=6.28318
  constraints (12):
    c: Vertical(g0)
    c: Coincident(g0,g1)
    c: Coincident(g1,g2)
    c: Horizontal(g2)
    c: Coincident(g2,g3)
    c: Coincident(g3,g4)
    c: Vertical(g4)
    c: Coincident(g4,g5)
    c: Coincident(g5,g6)
    c: Horizontal(g6)
    c: Coincident(g6,g7)
    c: Coincident(g7,g0)
FEATURE [Sketcher::SketchObject] Sketch033
  ArcFitTolerance = 1e-06
  AttachmentSupport = -> [Pocket012]
  ExternalGeometry = -> [Pocket012]
  FullyConstrained = false
  MakeInternals = false
  MapMode = 5
  Placement = pos=(0,47.4,0) rot=(0,0.707107,0.707107;3.14159rad)
  sketch-geometry (8):
    g0: LineSegment StartX=-14.6619 StartY=0 StartZ=0 EndX=-7.26206 EndY=0 EndZ=0
    g1: LineSegment StartX=-7.26206 StartY=0 StartZ=0 EndX=-7.26206 EndY=1.78706 EndZ=0
    g2: LineSegment StartX=-7.55642 StartY=2.08141 StartZ=0 EndX=-14.3676 EndY=2.08141 EndZ=0
    g3: LineSegment StartX=-14.6619 StartY=1.78706 StartZ=0 EndX=-14.6619 EndY=0 EndZ=0
    g4: ArcOfCircle CenterX=-14.3676 CenterY=1.78706 CenterZ=0 NormalX=0 NormalY=0 NormalZ=1 AngleXU=0 Radius=0.294356 StartAngle=1.5708 EndAngle=3.14159
    g5: GeomPoint [constr] X=-14.6619 Y=2.08141 Z=0
    g6: ArcOfCircle CenterX=-7.55642 CenterY=1.78706 CenterZ=0 NormalX=0 NormalY=0 NormalZ=1 AngleXU=0 Radius=0.294356 StartAngle=0 EndAngle=1.5708
    g7: GeomPoint [constr] X=-7.26206 Y=2.08141 Z=0
  constraints (15):
    c: Coincident(g0,g1)
    c: Coincident(g3,g0)
    c: Horizontal(g0)
    c: Horizontal(g2)
    c: Vertical(g1)
    c: Vertical(g3)
    c: PointOnObject(g0,g-3)
    c: PointOnObject(g5,g2)
    c: PointOnObject(g5,g3)
    c: Tangent(g2,g4) = -1.5708
    c: Tangent(g3,g4) = -1.5708
    c: PointOnObject(g7,g1)
    c: PointOnObject(g7,g2)
    c: Tangent(g1,g6) = -1.5708
    c: Tangent(g2,g6) = -1.5708
FEATURE [PartDesign::Pocket] Pocket
  BaseFeature = -> Pocket012
  Direction = (0,-1,2e-16)
  Length = 2
  Length2 = 5
  Profile = -> Sketch033
  ReferenceAxis = -> Sketch033 [N_Axis]
  Refine = true
  Suppressed = false
  Type = 0
FEATURE [PartDesign::Chamfer] Chamfer
  Angle = 45
  Base = -> Pocket [Edge34,Edge33]
  BaseFeature = -> Pocket
  ChamferType = 0
  FlipDirection = false
  Refine = true
  Size = 1
  Size2 = 1
  SupportTransform = false
  Suppressed = false
  UseAllEdges = false
FEATURE [PartDesign::Chamfer] Chamfer002
  Angle = 45
  Base = -> Chamfer [Edge5]
  BaseFeature = -> Chamfer
  ChamferType = 0
  FlipDirection = false
  Refine = true
  Size = 1.5
  Size2 = 1
  SupportTransform = false
  Suppressed = false
  UseAllEdges = false
FEATURE [PartDesign::Body] Body011  label="top"
  AllowCompound = false
  Group = -> [Sketch027,Pad014,Thickness001,Binder001,Sketch029,Pocket011,Binder002,Sketch030,Pad015,Sketch031,Pocket012,Sketch033,Pocket,Chamfer,Chamfer002]
  Origin = -> Origin023
  Tip = -> Chamfer002
FEATURE [App::Part] Part001  label="case"
  Group = -> [Body010,Body011]
  Origin = -> Origin021
FEATURE [App::Part] Board_58ce  label="thumb-cluster"
  Group = -> [Local_CS_58ce,Board_Geoms_58ce,Step_Models_58ce,Part001]
  Origin = -> Origin001
COMPONENT P3 — recipe-attached ("thumbstick-breakout", a linked part whose construction recipe lives in a companion FreeCAD document of the same project; that document's serialized recipe follows).
Construction recipe (the companion document, serialized — sketch geometry with constraints, then the solid features built on it; lengths are millimeters unless a unit is written):

FCSTD DOCUMENT  (FreeCAD 1.0RUnknown)
Label: thumbstick-breakout
License: All rights reserved
LicenseURL: https://en.wikipedia.org/wiki/All_rights_reserved
objects: Sketcher::SketchObject×14, App::Part×6, PartDesign::Pad×6, PartDesign::ShapeBinder×5, PartDesign::Pocket×5, PartDesign::Body×4, Part::Feature×3, PartDesign::Thickness×2, PartDesign::CoordinateSystem×1, Part::Ellipsoid×1, PartDesign::Plane×1, PartDesign::Chamfer×1, PartDesign::Revolution×1
note: 88 computed .brp shape members not serialized (recipe doc carries the construction recipe); baked Part::Feature solids carry a one-line shape summary decoded from their .brp

FEATURE [PartDesign::CoordinateSystem] Local_CS_bbd4
  AttacherType = Attacher::AttachEngine3D
  MapMode = 2
FEATURE [Part::Feature] Pcb_bbd4
  Placement = pos=(-137.3,117.78,0) rot=(0,0,1;0rad)
  shape: bbox 25.4 x 31.75 x 1.6 mm, 24 faces (baked)
FEATURE [Sketcher::SketchObject] PCB_Sketch_bbd4
  ArcFitTolerance = 1e-06
  FullyConstrained = false
  MakeInternals = false
  sketch-geometry (4):
    g0: LineSegment StartX=0 StartY=31.75 StartZ=0 EndX=0 EndY=0 EndZ=0
    g1: LineSegment StartX=25.4 StartY=31.75 StartZ=0 EndX=0 EndY=31.75 EndZ=0
    g2: LineSegment StartX=0 StartY=0 StartZ=0 EndX=25.4 EndY=0 EndZ=0
    g3: LineSegment StartX=25.4 StartY=0 StartZ=0 EndX=25.4 EndY=31.75 EndZ=0
  constraints (4):
    c: Coincident(g0,g2)
    c: Coincident(g0,g1)
    c: Coincident(g2,g3)
    c: Coincident(g1,g3)
FEATURE [App::Part] Board_Geoms_bbd4
  Group = -> [Pcb_bbd4,PCB_Sketch_bbd4]
  Origin = -> Origin
FEATURE [Part::Feature] Shape  label="J1_SOLID_4955641dfa02"
  Placement = pos=(12.66,29.4,0) rot=(0,0.707107,0.707107;3.14159rad)
  shape: bbox 4.001 x 3.601 x 0.9007 mm, 670 faces (baked)
FEATURE [App::Part] Top_bbd4
  Group = -> [Shape]
  Origin = -> Origin003
FEATURE [App::Part] Step_Models_bbd4
  Group = -> [Top_bbd4]
  Origin = -> Origin002
FEATURE [App::Part] Board_bbd4  label="thumbstick-breakout"
  Group = -> [Local_CS_bbd4,Board_Geoms_bbd4,Step_Models_bbd4]
  Origin = -> Origin001
FEATURE [Sketcher::SketchObject] Sketch009  label="2.005"
  ArcFitTolerance = 1e-06
  FullyConstrained = false
  MakeInternals = false
  sketch-geometry (8):
    g0: LineSegment StartX=-2.4 StartY=31.75 StartZ=0 EndX=-2.4 EndY=0 EndZ=0
    g1: ArcOfCircle CenterX=4.026e-13 CenterY=0 CenterZ=0 NormalX=0 NormalY=0 NormalZ=1 AngleXU=0 Radius=2.4 StartAngle=3.14159 EndAngle=4.71239
    g2: LineSegment StartX=4.70767e-08 StartY=-2.4 StartZ=0 EndX=25.4 EndY=-2.4 EndZ=0
    g3: ArcOfCircle CenterX=25.4 CenterY=0 CenterZ=0 NormalX=0 NormalY=0 NormalZ=1 AngleXU=0 Radius=2.4 StartAngle=4.71239 EndAngle=6.28318
    g4: LineSegment StartX=27.8 StartY=-7.37231e-07 StartZ=0 EndX=27.8 EndY=31.75 EndZ=0
    g5: ArcOfCircle CenterX=25.4 CenterY=31.75 CenterZ=0 NormalX=0 NormalY=0 NormalZ=1 AngleXU=0 Radius=2.4 StartAngle=0 EndAngle=1.5708
    g6: LineSegment StartX=25.4 StartY=34.15 StartZ=0 EndX=7.84308e-07 EndY=34.15 EndZ=0
    g7: ArcOfCircle CenterX=0 CenterY=31.75 CenterZ=0 NormalX=0 NormalY=0 NormalZ=1 AngleXU=0 Radius=2.4 StartAngle=1.5708 EndAngle=3.14159
  constraints (12):
    c: Vertical(g0)
    c: Coincident(g0,g1)
    c: Coincident(g1,g2)
    c: Horizontal(g2)
    c: Coincident(g2,g3)
    c: Coincident(g3,g4)
    c: Vertical(g4)
    c: Coincident(g4,g5)
    c: Coincident(g5,g6)
    c: Horizontal(g6)
    c: Coincident(g6,g7)
    c: Coincident(g7,g0)
FEATURE [PartDesign::Pad] Pad
  Direction = (0,0,1)
  Length = 3.2
  Length2 = 10
  Profile = -> Sketch009
  ReferenceAxis = -> Sketch009 [N_Axis]
  Refine = true
  Suppressed = false
  Type = 0
FEATURE [PartDesign::Thickness] Thickness001
  Base = -> Pad [Face10]
  BaseFeature = -> Pad
  Intersection = false
  Join = 0
  Mode = 0
  Refine = true
  Reversed = true
  SupportTransform = false
  Suppressed = false
  Value = 2
FEATURE [PartDesign::ShapeBinder] ShapeBinder
  Support = -> [Pcb_bbd4]
  TraceSupport = false
FEATURE [Sketcher::SketchObject] Sketch010
  ArcFitTolerance = 1e-06
  AttachmentSupport = -> [Thickness001]
  ExternalGeometry = -> [ShapeBinder]
  FullyConstrained = true
  MakeInternals = false
  MapMode = 5
  Placement = pos=(0,0,2) rot=(0,0,1;0rad)
  sketch-geometry (4):
    g0: Circle CenterX=2.54 CenterY=29.21 CenterZ=0 NormalX=0 NormalY=0 NormalZ=1 AngleXU=0 Radius=1.25
    g1: Circle CenterX=22.86 CenterY=29.21 CenterZ=0 NormalX=0 NormalY=0 NormalZ=1 AngleXU=0 Radius=1.25
    g2: Circle CenterX=22.86 CenterY=2.54 CenterZ=0 NormalX=0 NormalY=0 NormalZ=1 AngleXU=0 Radius=1.25
    g3: Circle CenterX=2.54 CenterY=2.54 CenterZ=0 NormalX=0 NormalY=0 NormalZ=1 AngleXU=0 Radius=1.25
  constraints (8):
    c: Diameter(g0) = 2.5
    c: Coincident(g0,g-3)
    c: Diameter(g1) = 2.5
    c: Coincident(g1,g-4)
    c: Diameter(g2) = 2.5
    c: Coincident(g2,g-5)
    c: Diameter(g3) = 2.5
    c: Coincident(g3,g-6)
FEATURE [PartDesign::Pocket] Pocket002
  BaseFeature = -> Thickness001
  Direction = (0,0,-1)
  Length = 5
  Length2 = 5
  Profile = -> Sketch010
  ReferenceAxis = -> Sketch010 [N_Axis]
  Refine = true
  Suppressed = false
  Type = 1
FEATURE [PartDesign::ShapeBinder] ShapeBinder003
  Support = -> [Pcb_bbd4]
  TraceSupport = false
FEATURE [Sketcher::SketchObject] Sketch011
  ArcFitTolerance = 1e-06
  AttachmentSupport = -> [Pocket002]
  ExternalGeometry = -> [ShapeBinder003]
  FullyConstrained = true
  MakeInternals = false
  MapMode = 5
  Placement = pos=(0,0,2) rot=(0,0,1;0rad)
  sketch-geometry (14):
    g0: Circle CenterX=9.45 CenterY=24.043 CenterZ=0 NormalX=0 NormalY=0 NormalZ=1 AngleXU=0 Radius=1.5
    g1: Circle CenterX=15.95 CenterY=24.043 CenterZ=0 NormalX=0 NormalY=0 NormalZ=1 AngleXU=0 Radius=1.5
    g2: Circle CenterX=15.95 CenterY=19.543 CenterZ=0 NormalX=0 NormalY=0 NormalZ=1 AngleXU=0 Radius=1.5
    g3: Circle CenterX=19.025 CenterY=18.793 CenterZ=0 NormalX=0 NormalY=0 NormalZ=1 AngleXU=0 Radius=1.5
    g4: Circle CenterX=19.025 CenterY=8.793 CenterZ=0 NormalX=0 NormalY=0 NormalZ=1 AngleXU=0 Radius=1.5
    g5: Circle CenterX=9.45 CenterY=19.543 CenterZ=0 NormalX=0 NormalY=0 NormalZ=1 AngleXU=0 Radius=1.5
    g6: Circle CenterX=6.375 CenterY=18.793 CenterZ=0 NormalX=0 NormalY=0 NormalZ=1 AngleXU=0 Radius=1.5
    g7: Circle CenterX=6.375 CenterY=8.793 CenterZ=0 NormalX=0 NormalY=0 NormalZ=1 AngleXU=0 Radius=1.5
    g8: Circle CenterX=3.97 CenterY=16.293 CenterZ=0 NormalX=0 NormalY=0 NormalZ=1 AngleXU=0 Radius=1.2
    g9: Circle CenterX=3.97 CenterY=13.793 CenterZ=0 NormalX=0 NormalY=0 NormalZ=1 AngleXU=0 Radius=1.2
    g10: Circle CenterX=3.97 CenterY=11.293 CenterZ=0 NormalX=0 NormalY=0 NormalZ=1 AngleXU=0 Radius=1.2
    g11: Circle CenterX=10.2 CenterY=5.063 CenterZ=0 NormalX=0 NormalY=0 NormalZ=1 AngleXU=0 Radius=1.2
    g12: Circle CenterX=12.7 CenterY=5.063 CenterZ=0 NormalX=0 NormalY=0 NormalZ=1 AngleXU=0 Radius=1.2
    g13: Circle CenterX=15.2 CenterY=5.063 CenterZ=0 NormalX=0 NormalY=0 NormalZ=1 AngleXU=0 Radius=1.2
  constraints (28):
    c: Diameter(g0) = 3
    c: Coincident(g0,g-3)
    c: Diameter(g1) = 3
    c: Coincident(g1,g-5)
    c: Diameter(g2) = 3
    c: Coincident(g2,g-6)
    c: Diameter(g3) = 3
    c: Coincident(g3,g-12)
    c: Diameter(g4) = 3
    c: Coincident(g4,g-13)
    c: Diameter(g5) = 3
    c: Coincident(g5,g-4)
    c: Diameter(g6) = 3
    c: Coincident(g6,g-7)
    c: Diameter(g7) = 3
    c: Coincident(g7,g-11)
    c: Diameter(g8) = 2.4
    c: Coincident(g8,g-8)
    c: Diameter(g9) = 2.4
    c: Coincident(g9,g-9)
    c: Diameter(g10) = 2.4
    c: Coincident(g10,g-10)
    c: Diameter(g11) = 2.4
    c: Coincident(g11,g-16)
    c: Diameter(g12) = 2.4
    c: Coincident(g12,g-15)
    c: Diameter(g13) = 2.4
    c: Coincident(g13,g-14)
FEATURE [PartDesign::Pocket] Pocket003
  BaseFeature = -> Pocket002
  Direction = (0,0,-1)
  Length = 1
  Length2 = 5
  Profile = -> Sketch011
  ReferenceAxis = -> Sketch011 [N_Axis]
  Refine = true
  Suppressed = false
  Type = 0
FEATURE [PartDesign::Body] Body  label="base"
  AllowCompound = false
  Group = -> [Sketch009,Pad,Thickness001,ShapeBinder,Sketch010,Pocket002,ShapeBinder003,Sketch011,Pocket003]
  Origin = -> Origin010
  Placement = pos=(0,0,-3.6) rot=(0,0,1;0rad)
  Tip = -> Pocket003
FEATURE [PartDesign::ShapeBinder] ShapeBinder004
  Placement = pos=(-137.3,117.78,0) rot=(0,0,1;0rad)
  Support = -> [Pcb_bbd4]
  TraceSupport = false
FEATURE [Sketcher::SketchObject] Sketch012
  ArcFitTolerance = 1e-06
  AttachmentSupport = -> [ShapeBinder004]
  ExternalGeometry = -> [ShapeBinder004]
  FullyConstrained = false
  MakeInternals = false
  MapMode = 5
  Placement = pos=(-137.3,117.78,0) rot=(0,0,1;0rad)
  sketch-geometry (15):
    g0: Circle CenterX=146.75 CenterY=-93.737 CenterZ=0 NormalX=0 NormalY=0 NormalZ=1 AngleXU=0 Radius=0.2
    g1: Circle CenterX=153.25 CenterY=-93.737 CenterZ=0 NormalX=0 NormalY=0 NormalZ=1 AngleXU=0 Radius=0.2
    g2: Circle CenterX=153.25 CenterY=-98.237 CenterZ=0 NormalX=0 NormalY=0 NormalZ=1 AngleXU=0 Radius=0.2
    g3: Circle CenterX=156.325 CenterY=-98.987 CenterZ=0 NormalX=0 NormalY=0 NormalZ=1 AngleXU=0 Radius=0.2
    g4: Circle CenterX=146.75 CenterY=-98.237 CenterZ=0 NormalX=0 NormalY=0 NormalZ=1 AngleXU=0 Radius=0.2
    g5: Circle CenterX=143.675 CenterY=-98.987 CenterZ=0 NormalX=0 NormalY=0 NormalZ=1 AngleXU=0 Radius=0.2
    g6: Circle CenterX=141.27 CenterY=-101.487 CenterZ=0 NormalX=0 NormalY=0 NormalZ=1 AngleXU=0 Radius=0.2
    g7: Circle CenterX=141.27 CenterY=-103.987 CenterZ=0 NormalX=0 NormalY=0 NormalZ=1 AngleXU=0 Radius=0.2
    g8: Circle CenterX=141.27 CenterY=-106.487 CenterZ=0 NormalX=0 NormalY=0 NormalZ=1 AngleXU=0 Radius=0.2
    g9: Circle CenterX=143.675 CenterY=-108.987 CenterZ=0 NormalX=0 NormalY=0 NormalZ=1 AngleXU=0 Radius=0.2
    g10: Circle CenterX=147.5 CenterY=-112.717 CenterZ=0 NormalX=0 NormalY=0 NormalZ=1 AngleXU=0 Radius=0.2
    g11: Circle CenterX=150 CenterY=-112.717 CenterZ=0 NormalX=0 NormalY=0 NormalZ=1 AngleXU=0 Radius=0.2
    g12: Circle CenterX=152.5 CenterY=-112.717 CenterZ=0 NormalX=0 NormalY=0 NormalZ=1 AngleXU=0 Radius=0.2
    g13: Circle CenterX=152.599 CenterY=-112.925 CenterZ=0 NormalX=0 NormalY=0 NormalZ=1 AngleXU=0 Radius=0.2
    g14: Circle CenterX=156.325 CenterY=-108.987 CenterZ=0 NormalX=0 NormalY=0 NormalZ=1 AngleXU=0 Radius=0.2
  constraints (15):
    c: Coincident(g0,g-3)
    c: Coincident(g1,g-4)
    c: Coincident(g2,g-5)
    c: Coincident(g3,g-6)
    c: Coincident(g4,g-7)
    c: Coincident(g5,g-8)
    c: Coincident(g6,g-9)
    c: Coincident(g7,g-10)
    c: Coincident(g8,g-11)
    c: Coincident(g9,g-12)
    c: Coincident(g10,g-13)
    c: Coincident(g11,g-14)
    c: Coincident(g14,g-16)
    c: Equal(g0, g1-g14) x14
    c: Radius(g0) = 0.2
FEATURE [Sketcher::SketchObject] Sketch013
  ArcFitTolerance = 1e-06
  AttachmentSupport = -> [XY_Plane012]
  ExternalGeometry = -> [ShapeBinder004]
  FullyConstrained = false
  MakeInternals = false
  MapMode = 5
  sketch-geometry (14):
    g0: LineSegment StartX=17.3886 StartY=25.1014 StartZ=0 EndX=8.04245 EndY=25.1014 EndZ=0
    g1: LineSegment StartX=6.375 StartY=18.793 StartZ=0 EndX=2.6831 EndY=18.793 EndZ=0
    g2: LineSegment StartX=2.6831 StartY=18.793 StartZ=0 EndX=2.6831 EndY=8.793 EndZ=0
    g3: LineSegment StartX=2.6831 StartY=8.793 StartZ=0 EndX=6.375 EndY=8.793 EndZ=0
    g4: LineSegment StartX=8.26567 StartY=4.26908 StartZ=0 EndX=16.6861 EndY=4.26908 EndZ=0
    g5: LineSegment StartX=16.6861 StartY=4.26908 StartZ=0 EndX=16.6861 EndY=8.793 EndZ=0
    g6: LineSegment StartX=16.6861 StartY=8.793 StartZ=0 EndX=19.025 EndY=8.793 EndZ=0
    g7: LineSegment StartX=19.025 StartY=8.793 StartZ=0 EndX=19.025 EndY=18.793 EndZ=0
    g8: LineSegment StartX=19.025 StartY=18.793 StartZ=0 EndX=17.3886 EndY=18.793 EndZ=0
    g9: LineSegment StartX=17.3886 StartY=18.793 StartZ=0 EndX=17.3886 EndY=25.1014 EndZ=0
    g10: LineSegment StartX=6.375 StartY=18.793 StartZ=0 EndX=8.04245 EndY=18.793 EndZ=0
    g11: LineSegment StartX=8.04245 StartY=18.793 StartZ=0 EndX=8.04245 EndY=25.1014 EndZ=0
    g12: LineSegment StartX=6.375 StartY=8.793 StartZ=0 EndX=8.26567 EndY=8.793 EndZ=0
    g13: LineSegment StartX=8.26567 StartY=8.793 StartZ=0 EndX=8.26567 EndY=4.26908 EndZ=0
  constraints (30):
    c: Horizontal(g0)
    c: Horizontal(g1)
    c: Coincident(g1,g2)
    c: Vertical(g2)
    c: Coincident(g2,g3)
    c: Horizontal(g3)
    c: Horizontal(g4)
    c: Coincident(g4,g5)
    c: Vertical(g5)
    c: Coincident(g5,g6)
    c: Horizontal(g6)
    c: Coincident(g6,g7)
    c: Coincident(g7,g8)
    c: Horizontal(g8)
    c: Coincident(g8,g9)
    c: Coincident(g9,g0)
    c: Vertical(g9)
    c: Coincident(g7,g-8)
    c: Coincident(g6,g-9)
    c: Coincident(g3,g-10)
    c: Coincident(g1,g10)
    c: Horizontal(g10)
    c: Coincident(g10,g11)
    c: Coincident(g11,g0)
    c: Vertical(g11)
    c: Coincident(g3,g12)
    c: Horizontal(g12)
    c: Coincident(g12,g13)
    c: Coincident(g13,g4)
    c: Vertical(g13)
FEATURE [PartDesign::Pad] Pad001
  Direction = (0,0,1)
  Length = 9.3
  Length2 = 10
  Profile = -> Sketch013
  ReferenceAxis = -> Sketch013 [N_Axis]
  Refine = true
  Suppressed = false
  Type = 0
FEATURE [PartDesign::Pad] Pad002
  BaseFeature = -> Pad001
  Direction = (0,0,1)
  Length = 2
  Length2 = 10
  Profile = -> Sketch012
  ReferenceAxis = -> Sketch012 [N_Axis]
  Refine = true
  Reversed = true
  Suppressed = false
  Type = 0
FEATURE [PartDesign::Body] Body001  label="Body"
  AllowCompound = false
  Group = -> [ShapeBinder004,Sketch012,Sketch013,Pad001,Pad002]
  Origin = -> Origin012
  Tip = -> Pad002
FEATURE [Sketcher::SketchObject] Sketch014  label="2.4"
  ArcFitTolerance = 1e-06
  FullyConstrained = false
  MakeInternals = false
  sketch-geometry (8):
    g0: LineSegment StartX=-2.4 StartY=31.75 StartZ=0 EndX=-2.4 EndY=0 EndZ=0
    g1: ArcOfCircle CenterX=0 CenterY=0 CenterZ=0 NormalX=0 NormalY=0 NormalZ=1 AngleXU=0 Radius=2.4 StartAngle=3.14159 EndAngle=4.71239
    g2: LineSegment StartX=-4e-16 StartY=-2.4 StartZ=0 EndX=25.4 EndY=-2.4 EndZ=0
    g3: ArcOfCircle CenterX=25.4 CenterY=0 CenterZ=0 NormalX=0 NormalY=0 NormalZ=1 AngleXU=1.5708 Radius=2.4 StartAngle=3.14159 EndAngle=4.71239
    g4: LineSegment StartX=27.8 StartY=-4e-16 StartZ=0 EndX=27.8 EndY=31.75 EndZ=0
    g5: ArcOfCircle CenterX=25.4 CenterY=31.75 CenterZ=0 NormalX=0 NormalY=0 NormalZ=1 AngleXU=-3.14159 Radius=2.4 StartAngle=3.14159 EndAngle=4.71239
    g6: LineSegment StartX=25.4 StartY=34.15 StartZ=0 EndX=0 EndY=34.15 EndZ=0
    g7: ArcOfCircle CenterX=0 CenterY=31.75 CenterZ=0 NormalX=0 NormalY=0 NormalZ=1 AngleXU=-1.5708 Radius=2.4 StartAngle=3.14159 EndAngle=4.71239
  constraints (12):
    c: Vertical(g0)
    c: Coincident(g0,g1)
    c: Coincident(g1,g2)
    c: Horizontal(g2)
    c: Coincident(g2,g3)
    c: Coincident(g3,g4)
    c: Vertical(g4)
    c: Coincident(g4,g5)
    c: Coincident(g5,g6)
    c: Horizontal(g6)
    c: Coincident(g6,g7)
    c: Coincident(g7,g0)
FEATURE [PartDesign::ShapeBinder] ShapeBinder005
  Support = -> [Pcb_bbd4]
  TraceSupport = false
FEATURE [Sketcher::SketchObject] Sketch
  ArcFitTolerance = 1e-06
  AttachmentSupport = -> [XY_Plane013]
  ExternalGeometry = -> [ShapeBinder005]
  FullyConstrained = true
  MakeInternals = false
  MapMode = 5
  sketch-geometry (2):
    g0: LineSegment [constr] StartX=6.375 StartY=18.793 StartZ=0 EndX=19.025 EndY=8.793 EndZ=0
    g1: Circle CenterX=12.7 CenterY=13.793 CenterZ=0 NormalX=0 NormalY=0 NormalZ=1 AngleXU=0 Radius=2
  constraints (4):
    c: Coincident(g0,g-3)
    c: Coincident(g0,g-5)
    c: Symmetric(g0,g0,g1)
    c: Diameter(g1) = 4
FEATURE [PartDesign::Pad] Pad003
  Direction = (0,0,1)
  Length = 12
  Length2 = 10
  Profile = -> Sketch
  ReferenceAxis = -> Sketch [N_Axis]
  Refine = true
  Suppressed = false
  Type = 0
FEATURE [PartDesign::Body] Body002  label="stick"
  AllowCompound = false
  Group = -> [ShapeBinder005,Sketch,Pad003]
  Origin = -> Origin013
  Placement = pos=(0,0,6.5) rot=(0,0,1;0rad)
  Tip = -> Pad003
FEATURE [Part::Feature] Part__Feature001  label="Thumbstick"
  Placement = pos=(12.7,13.8,-2.8) rot=(0,0,1;0rad)
  shape: bbox 24.74 x 24.74 x 17.5 mm, 20 faces (baked)
FEATURE [App::Part] Part  label="thumbstick"
  Group = -> [Body001,Body002,Part__Feature001]
  Origin = -> Origin011
FEATURE [Sketcher::SketchObject] Sketch015  label="2.006"
  ArcFitTolerance = 1e-06
  FullyConstrained = false
  MakeInternals = false
  sketch-geometry (8):
    g0: LineSegment StartX=-2.4 StartY=31.75 StartZ=0 EndX=-2.4 EndY=0 EndZ=0
    g1: ArcOfCircle CenterX=0 CenterY=0 CenterZ=0 NormalX=0 NormalY=0 NormalZ=1 AngleXU=0 Radius=2.4 StartAngle=3.14159 EndAngle=4.71239
    g2: LineSegment StartX=-4e-16 StartY=-2.4 StartZ=0 EndX=25.4 EndY=-2.4 EndZ=0
    g3: ArcOfCircle CenterX=25.4 CenterY=0 CenterZ=0 NormalX=0 NormalY=0 NormalZ=1 AngleXU=1.5708 Radius=2.4 StartAngle=3.14159 EndAngle=4.71239
    g4: LineSegment StartX=27.8 StartY=-7e-16 StartZ=0 EndX=27.8 EndY=31.75 EndZ=0
    g5: ArcOfCircle CenterX=25.4 CenterY=31.75 CenterZ=0 NormalX=0 NormalY=0 NormalZ=1 AngleXU=-3.14159 Radius=2.4 StartAngle=3.14159 EndAngle=4.71239
    g6: LineSegment StartX=25.4 StartY=34.15 StartZ=0 EndX=0 EndY=34.15 EndZ=0
    g7: ArcOfCircle CenterX=0 CenterY=31.75 CenterZ=0 NormalX=0 NormalY=0 NormalZ=1 AngleXU=-1.5708 Radius=2.4 StartAngle=3.14159 EndAngle=4.71239
  constraints (12):
    c: Vertical(g0)
    c: Coincident(g0,g1)
    c: Coincident(g1,g2)
    c: Horizontal(g2)
    c: Coincident(g2,g3)
    c: Coincident(g3,g4)
    c: Vertical(g4)
    c: Coincident(g4,g5)
    c: Coincident(g5,g6)
    c: Horizontal(g6)
    c: Coincident(g6,g7)
    c: Coincident(g7,g0)
FEATURE [PartDesign::Pad] Pad004
  Direction = (0,0,1)
  Length = 5.3
  Length2 = 10
  Profile = -> Sketch015
  ReferenceAxis = -> Sketch015 [N_Axis]
  Refine = true
  Suppressed = false
  Type = 0
FEATURE [PartDesign::Thickness] Thickness
  Base = -> Pad004 [Face9]
  BaseFeature = -> Pad004
  Intersection = false
  Join = 0
  Mode = 0
  Refine = true
  Reversed = true
  SupportTransform = false
  Suppressed = false
  Value = 2
FEATURE [PartDesign::ShapeBinder] ShapeBinder006
  Support = -> [Pocket003]
  TraceSupport = false
FEATURE [Sketcher::SketchObject] Sketch016
  ArcFitTolerance = 1e-06
  AttachmentSupport = -> [Thickness]
  ExternalGeometry = -> [ShapeBinder006]
  FullyConstrained = true
  MakeInternals = false
  MapMode = 5
  Placement = pos=(0,0,0) rot=(1,0,0;3.14159rad)
  sketch-geometry (8):
    g0: Circle CenterX=2.54 CenterY=-2.54 CenterZ=0 NormalX=0 NormalY=0 NormalZ=1 AngleXU=0 Radius=3
    g1: Circle CenterX=22.86 CenterY=-2.54 CenterZ=0 NormalX=0 NormalY=0 NormalZ=1 AngleXU=0 Radius=3
    g2: Circle CenterX=22.86 CenterY=-29.21 CenterZ=0 NormalX=0 NormalY=0 NormalZ=1 AngleXU=0 Radius=3
    g3: Circle CenterX=2.54 CenterY=-29.21 CenterZ=0 NormalX=0 NormalY=0 NormalZ=1 AngleXU=0 Radius=3
    g4: Circle CenterX=2.54 CenterY=-2.54 CenterZ=0 NormalX=0 NormalY=0 NormalZ=1 AngleXU=0 Radius=1.65
    g5: Circle CenterX=22.86 CenterY=-2.54 CenterZ=0 NormalX=0 NormalY=0 NormalZ=1 AngleXU=0 Radius=1.65
    g6: Circle CenterX=22.86 CenterY=-29.21 CenterZ=0 NormalX=0 NormalY=0 NormalZ=1 AngleXU=0 Radius=1.65
    g7: Circle CenterX=2.54 CenterY=-29.21 CenterZ=0 NormalX=0 NormalY=0 NormalZ=1 AngleXU=0 Radius=1.65
  constraints (16):
    c: Diameter(g0) = 6
    c: Coincident(g0,g-3)
    c: Diameter(g1) = 6
    c: Coincident(g1,g-4)
    c: Diameter(g2) = 6
    c: Coincident(g2,g-5)
    c: Diameter(g3) = 6
    c: Coincident(g3,g-6)
    c: Diameter(g4) = 3.3
    c: Coincident(g4,g0)
    c: Diameter(g5) = 3.3
    c: Coincident(g5,g1)
    c: Diameter(g6) = 3.3
    c: Coincident(g6,g2)
    c: Diameter(g7) = 3.3
    c: Coincident(g7,g3)
FEATURE [Part::Ellipsoid] Ellipsoid
  Angle1 = -90
  Angle2 = 90
  Angle3 = 180
  AttacherType = Attacher::AttachEngine3D
  Placement = pos=(12.7,13.8,9.3) rot=(1,0,0;1.5708rad)
  Radius1 = 12.37
  Radius2 = 12.37
  Radius3 = 8
FEATURE [PartDesign::Plane] DatumPlane
  AttachmentOffset = pos=(0,0,12.7) rot=(0,0,1;0rad)
  AttachmentSupport = -> [YZ_Plane014]
  Length = 70.0266
  MapMode = 5
  Placement = pos=(12.7,0,0) rot=(0.57735,0.57735,0.57735;2.0944rad)
  ResizeMode = 0
  Width = 60.8766
FEATURE [Sketcher::SketchObject] Sketch017
  ArcFitTolerance = 1e-06
  AttachmentSupport = -> [DatumPlane]
  FullyConstrained = false
  MakeInternals = false
  MapMode = 5
  Placement = pos=(12.7,0,0) rot=(0.57735,0.57735,0.57735;2.0944rad)
  sketch-geometry (18):
    g0: Circle [constr] CenterX=29.1118 CenterY=3.8 CenterZ=0 NormalX=0 NormalY=0 NormalZ=1 AngleXU=0 Radius=1
    g1: Circle [constr] CenterX=30.0485 CenterY=13.7535 CenterZ=0 NormalX=0 NormalY=0 NormalZ=1 AngleXU=0 Radius=1
    g2: Circle [constr] CenterX=23.3909 CenterY=17.1877 CenterZ=0 NormalX=0 NormalY=0 NormalZ=1 AngleXU=0 Radius=1
    g3: BSplineCurve PolesCount=3 KnotsCount=2 Degree=2 IsPeriodic=0
    g4: GeomPoint [constr] X=29.1118 Y=3.8 Z=0
    g5: GeomPoint [constr] X=23.3909 Y=17.1877 Z=0
    g6: LineSegment StartX=23.3909 StartY=17.1877 StartZ=0 EndX=13.7824 EndY=17.1877 EndZ=0
    g7: Circle [constr] CenterX=28.1118 CenterY=3.8 CenterZ=0 NormalX=0 NormalY=0 NormalZ=1 AngleXU=0 Radius=1
    g8: Circle [constr] CenterX=28.4002 CenterY=12.6207 CenterZ=0 NormalX=0 NormalY=0 NormalZ=1 AngleXU=0 Radius=1
    g9: Circle [constr] CenterX=23.1917 CenterY=16.2077 CenterZ=0 NormalX=0 NormalY=0 NormalZ=1 AngleXU=0 Radius=1
    g10: BSplineCurve PolesCount=3 KnotsCount=2 Degree=2 IsPeriodic=0
    g11: GeomPoint [constr] X=28.1118 Y=3.8 Z=0
    g12: GeomPoint [constr] X=23.1917 Y=16.2077 Z=0
    g13: LineSegment StartX=28.1118 StartY=3.8 StartZ=0 EndX=29.1118 EndY=3.8 EndZ=0
    g14: LineSegment StartX=13.7824 StartY=17.1877 StartZ=0 EndX=13.7824 EndY=16.2077 EndZ=0
    g15: LineSegment StartX=13.7824 StartY=16.2077 StartZ=0 EndX=23.1917 EndY=16.2077 EndZ=0
    g16: LineSegment [constr] StartX=1.40969 StartY=9.23031 StartZ=0 EndX=26.155 EndY=9.23031 EndZ=0
    g17: LineSegment [constr] StartX=13.7824 StartY=9.23031 StartZ=0 EndX=13.7824 EndY=17.9973 EndZ=0
  constraints (33):
    c: Weight(g0) = 1
    c: Equal(g0,g1)
    c: Equal(g0,g2)
    c: InternalAlignment(g0,g3)
    c: InternalAlignment(g1,g3)
    c: InternalAlignment(g2,g3)
    c: InternalAlignment(g4,g3)
    c: InternalAlignment(g5,g3)
    c: Coincident(g6,g3)
    c: Horizontal(g6)
    c: Weight(g7) = 1
    c: Equal(g7,g8)
    c: Equal(g7,g9)
    c: InternalAlignment(g7,g10)
    c: InternalAlignment(g8,g10)
    c: InternalAlignment(g9,g10)
    c: InternalAlignment(g11,g10)
    c: InternalAlignment(g12,g10)
    c: Coincident(g13,g10)
    c: Coincident(g13,g3)
    c: Horizontal(g13)
    c: DistanceX(g13,g13) = 1
    c: Distance(g3,g10) = 1
    c: Distance(g1,g8) = 2
    c: Coincident(g6,g14)
    c: Vertical(g14)
    c: Coincident(g15,g10)
    c: Horizontal(g15)
    c: Horizontal(g16)
    c: Symmetric(g16,g16,g17)
    c: Vertical(g17)
    c: PointOnObject(g6,g17)
    c: Distance(g10,g-3) = 1.5
FEATURE [PartDesign::Chamfer] Chamfer
  Angle = 45
  Base = -> Thickness [Edge4]
  BaseFeature = -> Thickness
  ChamferType = 0
  FlipDirection = false
  Refine = true
  Size = 1.5
  Size2 = 1
  SupportTransform = false
  Suppressed = false
  UseAllEdges = false
FEATURE [PartDesign::Pad] Pad005
  BaseFeature = -> Chamfer
  Direction = (0,0,-1)
  Length = 3.3
  Length2 = 10
  Profile = -> Sketch016
  ReferenceAxis = -> Sketch016 [N_Axis]
  Refine = true
  Reversed = true
  Suppressed = false
  Type = 0
FEATURE [PartDesign::Revolution] Revolution
  Angle = 360
  Angle2 = 60
  Axis = (0,0,-1)
  Base = (12.7,13.7824,17.1877)
  BaseFeature = -> Pad005
  Profile = -> Sketch017
  ReferenceAxis = -> Sketch017 [Edge4]
  Refine = true
  Reversed = true
  Suppressed = false
  Type = 0
FEATURE [Sketcher::SketchObject] Sketch018
  ArcFitTolerance = 1e-06
  AttachmentSupport = -> [Revolution]
  ExternalGeometry = -> [Revolution]
  FullyConstrained = true
  MakeInternals = false
  MapMode = 5
  Placement = pos=(0,0,17.1877) rot=(0,0,1;0rad)
  sketch-geometry (1):
    g0: Circle CenterX=12.7 CenterY=13.7824 CenterZ=0 NormalX=0 NormalY=0 NormalZ=1 AngleXU=0 Radius=9.5
  constraints (2):
    c: Coincident(g0,g-3)
    c: Diameter(g0) = 19
FEATURE [PartDesign::Pocket] Pocket
  BaseFeature = -> Revolution
  Direction = (0,0,-1)
  Length = 14
  Length2 = 5
  Profile = -> Sketch018
  ReferenceAxis = -> Sketch018 [N_Axis]
  Refine = true
  Suppressed = false
  Type = 0
FEATURE [Sketcher::SketchObject] Sketch019
  ArcFitTolerance = 1e-06
  AttachmentSupport = -> [Pocket]
  FullyConstrained = true
  MakeInternals = false
  MapMode = 5
  Placement = pos=(0,0,5.3) rot=(0,0,1;0rad)
  sketch-geometry (1):
    g0: Circle CenterX=12.7 CenterY=13.7824 CenterZ=0 NormalX=0 NormalY=0 NormalZ=1 AngleXU=0 Radius=14.157
  constraints (2):
    c: Coincident(g0,g-3)
    c: Equal(g0,g-3)
FEATURE [PartDesign::Pocket] Pocket004
  BaseFeature = -> Pocket
  Direction = (0,0,-1)
  Length = 2
  Length2 = 5
  Profile = -> Sketch019
  ReferenceAxis = -> Sketch019 [N_Axis]
  Refine = true
  Suppressed = false
  Type = 0
FEATURE [Sketcher::SketchObject] Sketch020
  ArcFitTolerance = 1e-06
  AttachmentSupport = -> [Pocket004]
  ExternalGeometry = -> [Pocket004]
  FullyConstrained = false
  MakeInternals = false
  MapMode = 5
  Placement = pos=(0,34.15,0) rot=(0,0.707107,0.707107;3.14159rad)
  sketch-geometry (4):
    g0: LineSegment StartX=-15.1629 StartY=0 StartZ=0 EndX=-10.1629 EndY=0 EndZ=0
    g1: LineSegment StartX=-10.1629 StartY=0 StartZ=0 EndX=-10.1629 EndY=1.3 EndZ=0
    g2: LineSegment StartX=-10.1629 StartY=1.3 StartZ=0 EndX=-15.1629 EndY=1.3 EndZ=0
    g3: LineSegment StartX=-15.1629 StartY=1.3 StartZ=0 EndX=-15.1629 EndY=0 EndZ=0
  constraints (11):
    c: Coincident(g0,g1)
    c: Coincident(g1,g2)
    c: Coincident(g2,g3)
    c: Coincident(g3,g0)
    c: Horizontal(g0)
    c: Horizontal(g2)
    c: Vertical(g1)
    c: Vertical(g3)
    c: PointOnObject(g0,g-3)
    c: DistanceX(g2,g2) = 5
    c: DistanceY(g1,g1) = 1.3
FEATURE [PartDesign::Pocket] Pocket005
  BaseFeature = -> Pocket004
  Direction = (0,-1,2e-16)
  Length = 2
  Length2 = 5
  Profile = -> Sketch020
  ReferenceAxis = -> Sketch020 [N_Axis]
  Refine = true
  Suppressed = false
  Type = 0
FEATURE [PartDesign::Body] Body003  label="top"
  AllowCompound = false
  Group = -> [Sketch015,Pad004,Thickness,Chamfer,ShapeBinder006,Sketch016,Pad005,DatumPlane,Sketch017,Revolution,Sketch018,Pocket,Sketch019,Pocket004,Sketch020,Pocket005]
  Origin = -> Origin014
  Tip = -> Pocket005
FEATURE [App::Part] Part001  label="case"
  Group = -> [Body,Body003,Ellipsoid]
  Origin = -> Origin009
PROVENANCE & LICENSES
A FreeCAD (.FCStd) document from a public repository crawl; recipes are the document's own serialized feature recipes (and, for linked parts, companion documents' recipes).
License: gpl-3.0.
